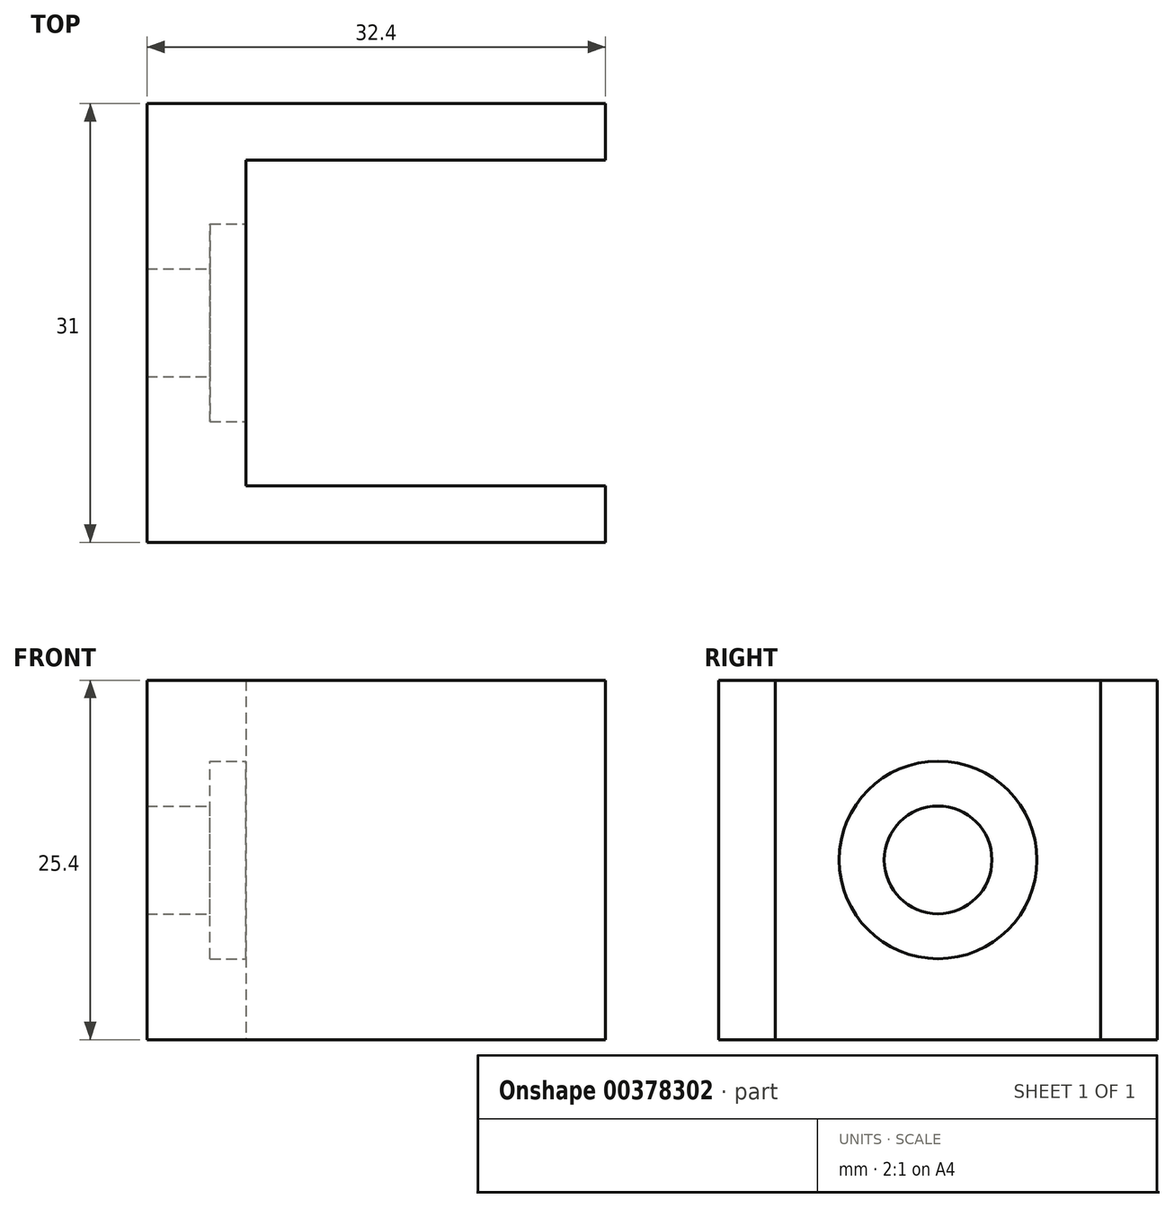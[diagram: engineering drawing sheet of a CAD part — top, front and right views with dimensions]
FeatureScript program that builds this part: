
annotation { "Feature Type Name" : "Feature", "Feature Type Description" : "" }
export const myFeature = defineFeature(function(context is Context, id is Id, definition is map)
    precondition{}
    {
        {
            var Q0;
            Q0=qCreatedBy(makeId("Top.planeOp"),FACE);
            var sketch = newSketch(context, id + "F0", { "sketchPlane" : qUnion([Q0])});
            skLineSegment(sketch, "E0", {"start": v(-19.33, 21.18) * mm, "end": v(-19.33, -1.82) * mm});
            skLineSegment(sketch, "E1", {"start": v(-19.33, -1.82) * mm, "end": v(6.07, -1.82) * mm});
            skLineSegment(sketch, "E2", {"start": v(-19.33, 21.18) * mm, "end": v(6.07, 21.18) * mm});
            skLineSegment(sketch, "E3.0", {"start": v(-26.33, 25.18) * mm, "end": v(-26.33, -5.82) * mm});
            skLineSegment(sketch, "E4.0", {"start": v(-26.33, 25.18) * mm, "end": v(6.07, 25.18) * mm});
            skLineSegment(sketch, "E5.0", {"start": v(-26.33, -5.82) * mm, "end": v(6.07, -5.82) * mm});
            skLineSegment(sketch, "E6", {"start": v(6.07, 25.18) * mm, "end": v(6.07, 21.18) * mm});
            skLineSegment(sketch, "E7", {"start": v(6.07, -1.82) * mm, "end": v(6.07, -5.82) * mm});
            skSolve(sketch);
        }
        {
            var Q0;
            Q0 = qSketchRegion(id + "F0", true);
            extrude(context, id + "F1", {"entities" : qUnion([Q0]), "depth" : 25.4 * mm});
        }
        {
            var Q0;
            Q0=makeQuery(id+"F1.opExtrude","SWEPT_FACE",FACE,{"disambiguationData":[OSD([sQuery(id+"F0.wireOp",EDGE,"E0")])]});
            var sketch = newSketch(context, id + "F2", { "sketchPlane" : qUnion([Q0])});
            skLineSegment(sketch, "E8", {"start": v(9.68, 0) * mm, "end": v(9.68, 25.4) * mm, "construction": true});
            skLineSegment(sketch, "E9", {"start": v(21.18, 12.7) * mm, "end": v(-1.82, 12.7) * mm, "construction": true});
            skCircle(sketch, "E10", {"center": v(9.68, 12.7) * mm, "radius": 6.99 * mm});
            skCircle(sketch, "E11", {"center": v(9.68, 12.7) * mm, "radius": 3.81 * mm});
            skSolve(sketch);
        }
        {
            var Q0;
            Q0=makeQuery(id+"F2.imprint","IMPRINT",FACE,{"disambiguationData":[TD([[makeQuery(id+"F2.imprint","IMPRINT",EDGE,{"derivedFrom":sQuery(id+"F2.wireOp",EDGE,"E10")}),1.0]])]});
            var Q1;
            Q1=makeQuery(id+"F2.imprint","IMPRINT",FACE,{"disambiguationData":[TD([[makeQuery(id+"F2.imprint","IMPRINT",EDGE,{"derivedFrom":sQuery(id+"F2.wireOp",EDGE,"E11")}),1.0]])]});
            extrude(context, id + "F3", {"entities" : qUnion([Q0, Q1]), "operationType" : NewBodyOperationType.REMOVE, "oppositeDirection" : true, "depth" : 2.54 * mm});
        }
        {
            var Q0;
            Q0=makeQuery(id+"F2.imprint","IMPRINT",FACE,{"disambiguationData":[TD([[makeQuery(id+"F2.imprint","IMPRINT",EDGE,{"derivedFrom":sQuery(id+"F2.wireOp",EDGE,"E11")}),1.0]])]});
            var Q1;
            Q1=makeQuery(id+"F1.opExtrude","SWEPT_FACE",FACE,{"disambiguationData":[OSD([sQuery(id+"F0.wireOp",EDGE,"E3.0")])]});
            extrude(context, id + "F4", {"entities" : qUnion([Q0]), "operationType" : NewBodyOperationType.REMOVE, "endBound" : BoundingType.UP_TO_SURFACE, "oppositeDirection" : true, "endBoundEntityFace" : qUnion([Q1]), "depth" : 25.4 * mm});
        }
    });
